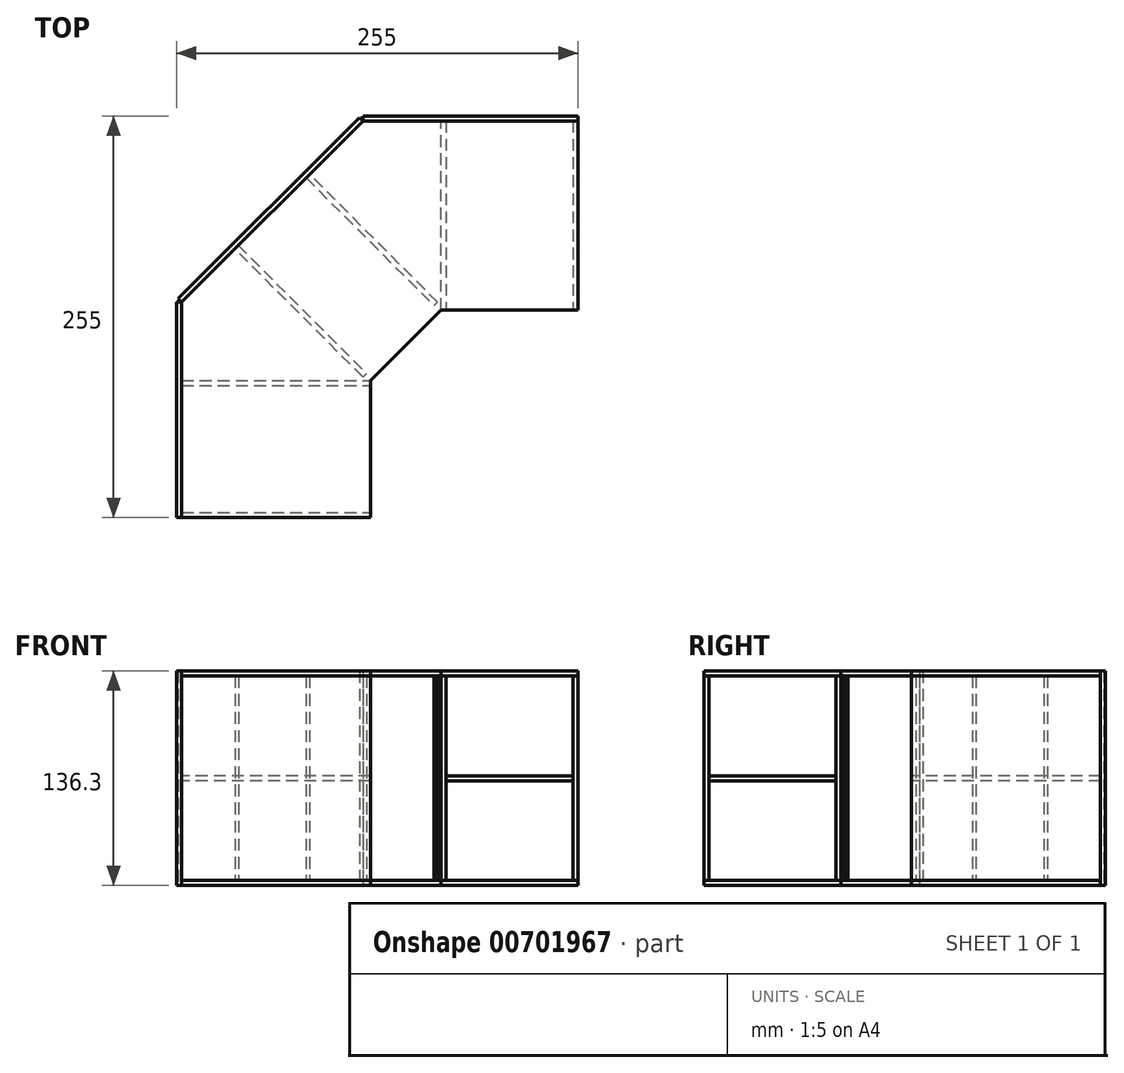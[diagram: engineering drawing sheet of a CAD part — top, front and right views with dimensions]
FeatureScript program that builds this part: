
annotation { "Feature Type Name" : "Feature", "Feature Type Description" : "" }
export const myFeature = defineFeature(function(context is Context, id is Id, definition is map)
    precondition{}
    {
        {
            assignVariable(context, id + "F0", {"name" : "x", "anyValue" : 3.15});
        }
        {
            var Q0;
            Q0=qCreatedBy(makeId("Top.planeOp"),FACE);
            var sketch = newSketch(context, id + "F1", { "sketchPlane" : qUnion([Q0])});
            skLineSegment(sketch, "E0", {"start": v(0, 0) * mm, "end": v(120, 0) * mm});
            skLineSegment(sketch, "E1", {"start": v(120, 0) * mm, "end": v(120, 87) * mm});
            skLineSegment(sketch, "E2", {"start": v(120, 87) * mm, "end": v(164.85, 131.85) * mm});
            skLineSegment(sketch, "E3", {"start": v(164.85, 131.85) * mm, "end": v(251.85, 131.85) * mm});
            skLineSegment(sketch, "E4", {"start": v(251.85, 131.85) * mm, "end": v(251.85, 251.85) * mm});
            skLineSegment(sketch, "E5", {"start": v(251.85, 251.85) * mm, "end": v(115.14, 251.85) * mm});
            skLineSegment(sketch, "E6", {"start": v(115.14, 251.85) * mm, "end": v(0, 136.7) * mm});
            skLineSegment(sketch, "E7", {"start": v(0, 136.7) * mm, "end": v(0, 0) * mm});
            skLineSegment(sketch, "E8", {"start": v(0, 136.7) * mm, "end": v(0, 251.85) * mm, "construction": true});
            skLineSegment(sketch, "E9", {"start": v(0, 251.85) * mm, "end": v(115.14, 251.85) * mm, "construction": true});
            skLineSegment(sketch, "E10", {"start": v(251.85, 131.85) * mm, "end": v(251.85, 0) * mm, "construction": true});
            skLineSegment(sketch, "E11", {"start": v(251.85, 0) * mm, "end": v(120, 0) * mm, "construction": true});
            skLineSegment(sketch, "E12", {"start": v(251.85, 0) * mm, "end": v(142.42, 109.42) * mm, "construction": true});
            skLineSegment(sketch, "E13", {"start": v(142.43, 109.42) * mm, "end": v(57.57, 194.28) * mm, "construction": true});
            skLineSegment(sketch, "E14", {"start": v(57.57, 194.28) * mm, "end": v(0, 251.85) * mm, "construction": true});
            skLineSegment(sketch, "E15.0", {"start": v(-3.15, 104.14) * mm, "end": v(-3.15, 0) * mm});
            skSolve(sketch);
        }
        {
            var Q0;
            Q0 = qSketchRegion(id + "F1", true);
            extrude(context, id + "F2", {"entities" : qUnion([Q0]), "depth" : (getVariable(context, 'x')) * mm, "offsetDistance" : 25 * mm});
        }
        {
            var Q0;
            Q0=makeQuery(id+"F2.opExtrude","SWEPT_FACE",FACE,{"disambiguationData":[OSD([sQuery(id+"F1.wireOp",EDGE,"E0")])]});
            var sketch = newSketch(context, id + "F3", { "sketchPlane" : qUnion([Q0])});
            skLineSegment(sketch, "E16.bottom", {"start": v(0, 0) * mm, "end": v(120, 0) * mm});
            skLineSegment(sketch, "E16.top", {"start": v(0, -130) * mm, "end": v(120, -130) * mm});
            skLineSegment(sketch, "E16.left", {"start": v(0, 0) * mm, "end": v(0, -130) * mm});
            skLineSegment(sketch, "E16.right", {"start": v(120, 0) * mm, "end": v(120, -130) * mm});
            skSolve(sketch);
        }
        {
            var Q0;
            Q0 = qSketchRegion(id + "F3", true);
            extrude(context, id + "F4", {"entities" : qUnion([Q0]), "oppositeDirection" : true, "depth" : (getVariable(context, 'x')) * mm, "offsetDistance" : 25 * mm});
        }
        {
            var Q0;
            Q0=makeQuery(id+"F4.opExtrude","SWEPT_BODY",BODY,{"disambiguationData":[OSD([sQuery(id+"F3.wireOp",EDGE,"E16.bottom"),sQuery(id+"F3.wireOp",EDGE,"E16.top"),sQuery(id+"F3.wireOp",EDGE,"E16.left"),sQuery(id+"F3.wireOp",EDGE,"E16.right")])]});
            transform(context, id + "F5", {"entities" : qUnion([Q0]), "transformType" : TransformType.TRANSLATION_3D, "dx" : 0 * mm, "dy" : 83.9 * mm, "dz" : 0 * mm, "makeCopy" : true});
        }
        {
            var Q0;
            Q0=makeQuery(id+"F2.opExtrude","SWEPT_FACE",FACE,{"disambiguationData":[OSD([sQuery(id+"F1.wireOp",EDGE,"E4")])]});
            var sketch = newSketch(context, id + "F6", { "sketchPlane" : qUnion([Q0])});
            skLineSegment(sketch, "E17.bottom", {"start": v(131.85, 0) * mm, "end": v(251.85, 0) * mm});
            skLineSegment(sketch, "E17.top", {"start": v(131.85, -130) * mm, "end": v(251.85, -130) * mm});
            skLineSegment(sketch, "E17.left", {"start": v(131.85, 0) * mm, "end": v(131.85, -130) * mm});
            skLineSegment(sketch, "E17.right", {"start": v(251.85, 0) * mm, "end": v(251.85, -130) * mm});
            skSolve(sketch);
        }
        {
            var Q0;
            Q0 = qSketchRegion(id + "F6", true);
            extrude(context, id + "F7", {"entities" : qUnion([Q0]), "oppositeDirection" : true, "depth" : (getVariable(context, 'x')) * mm, "offsetDistance" : 25 * mm});
        }
        {
            var Q0;
            Q0=makeQuery(id+"F7.opExtrude","SWEPT_BODY",BODY,{"disambiguationData":[OSD([sQuery(id+"F6.wireOp",EDGE,"E17.bottom"),sQuery(id+"F6.wireOp",EDGE,"E17.top"),sQuery(id+"F6.wireOp",EDGE,"E17.left"),sQuery(id+"F6.wireOp",EDGE,"E17.right")])]});
            transform(context, id + "F8", {"entities" : qUnion([Q0]), "transformType" : TransformType.TRANSLATION_3D, "dx" : -83.9 * mm, "dy" : 0 * mm, "dz" : 0 * mm, "makeCopy" : true});
        }
        {
            var Q0;
            Q0=makeQuery(id+"F2.opExtrude","SWEPT_BODY",BODY,{"disambiguationData":[OSD([sQuery(id+"F1.wireOp",EDGE,"E0"),sQuery(id+"F1.wireOp",EDGE,"E1"),sQuery(id+"F1.wireOp",EDGE,"E2"),sQuery(id+"F1.wireOp",EDGE,"E3"),sQuery(id+"F1.wireOp",EDGE,"E4"),sQuery(id+"F1.wireOp",EDGE,"E5"),sQuery(id+"F1.wireOp",EDGE,"E6"),sQuery(id+"F1.wireOp",EDGE,"E7")])]});
            transform(context, id + "F9", {"entities" : qUnion([Q0]), "transformType" : TransformType.TRANSLATION_3D, "dx" : 0 * mm, "dy" : 0 * mm, "dz" : (-130 - 3.15) * mm, "makeCopy" : true});
        }
        {
            var Q0;
            Q0=makeQuery(id+"F9.opPattern","COPY",FACE,{"derivedFrom":makeQuery(id+"F2.opExtrude","CAP_FACE",FACE,{"disambiguationData":[OSD([sQuery(id+"F1.wireOp",EDGE,"E0"),sQuery(id+"F1.wireOp",EDGE,"E1"),sQuery(id+"F1.wireOp",EDGE,"E2"),sQuery(id+"F1.wireOp",EDGE,"E3"),sQuery(id+"F1.wireOp",EDGE,"E4"),sQuery(id+"F1.wireOp",EDGE,"E5"),sQuery(id+"F1.wireOp",EDGE,"E6"),sQuery(id+"F1.wireOp",EDGE,"E7")])],"isStart":false}),"instanceName":"1"});
            cPlane(context, id + "F10", {"entities" : qUnion([Q0]), "cplaneType" : CPlaneType.OFFSET, "offset" : 63.42 * mm, "width" : 150 * mm, "height" : 150 * mm});
        }
        {
            var Q0;
            Q0=qCreatedBy(id+"F10.planeOp",FACE);
            var sketch = newSketch(context, id + "F11", { "sketchPlane" : qUnion([Q0])});
            skLineSegment(sketch, "E18.bottom", {"start": v(120, 3.15) * mm, "end": v(0, 3.15) * mm});
            skLineSegment(sketch, "E18.top", {"start": v(120, 83.9) * mm, "end": v(0, 83.9) * mm});
            skLineSegment(sketch, "E18.left", {"start": v(120, 3.15) * mm, "end": v(120, 83.9) * mm});
            skLineSegment(sketch, "E18.right", {"start": v(0, 3.15) * mm, "end": v(0, 83.9) * mm});
            skLineSegment(sketch, "E19.bottom", {"start": v(167.95, 251.85) * mm, "end": v(248.7, 251.85) * mm});
            skLineSegment(sketch, "E19.top", {"start": v(167.95, 131.85) * mm, "end": v(248.7, 131.85) * mm});
            skLineSegment(sketch, "E19.left", {"start": v(167.95, 251.85) * mm, "end": v(167.95, 131.85) * mm});
            skLineSegment(sketch, "E19.right", {"start": v(248.7, 251.85) * mm, "end": v(248.7, 131.85) * mm});
            skSolve(sketch);
        }
        {
            var Q0;
            Q0 = qSketchRegion(id + "F11", true);
            extrude(context, id + "F12", {"entities" : qUnion([Q0]), "depth" : (getVariable(context, 'x')) * mm, "offsetDistance" : 25 * mm});
        }
        {
            var Q0;
            Q0=makeQuery(id+"F9.opPattern","COPY",FACE,{"derivedFrom":makeQuery(id+"F2.opExtrude","CAP_FACE",FACE,{"disambiguationData":[OSD([sQuery(id+"F1.wireOp",EDGE,"E0"),sQuery(id+"F1.wireOp",EDGE,"E1"),sQuery(id+"F1.wireOp",EDGE,"E2"),sQuery(id+"F1.wireOp",EDGE,"E3"),sQuery(id+"F1.wireOp",EDGE,"E4"),sQuery(id+"F1.wireOp",EDGE,"E5"),sQuery(id+"F1.wireOp",EDGE,"E6"),sQuery(id+"F1.wireOp",EDGE,"E7")])],"isStart":false}),"instanceName":"1"});
            var sketch = newSketch(context, id + "F13", { "sketchPlane" : qUnion([Q0])});
            skLineSegment(sketch, "E20", {"start": v(117.4, 91.46) * mm, "end": v(36.08, 172.78) * mm});
            skLineSegment(sketch, "E21", {"start": v(36.08, 172.78) * mm, "end": v(33.85, 170.55) * mm});
            skLineSegment(sketch, "E22", {"start": v(33.85, 170.55) * mm, "end": v(115.17, 89.24) * mm});
            skLineSegment(sketch, "E23", {"start": v(115.17, 89.24) * mm, "end": v(117.4, 91.46) * mm});
            skLineSegment(sketch, "E24", {"start": v(117.4, 91.46) * mm, "end": v(120.93, 87.93) * mm, "construction": true});
            skLineSegment(sketch, "E25", {"start": v(142.42, 109.42) * mm, "end": v(57.57, 194.28) * mm, "construction": true});
            skLineSegment(sketch, "E26.MirrorCS", {"start": v(79.07, 215.77) * mm, "end": v(81.3, 218) * mm});
            skLineSegment(sketch, "E27.MirrorCS", {"start": v(162.61, 136.68) * mm, "end": v(160.39, 134.46) * mm});
            skLineSegment(sketch, "E28.MirrorCS", {"start": v(81.3, 218) * mm, "end": v(162.61, 136.68) * mm});
            skLineSegment(sketch, "E29.MirrorCS", {"start": v(160.39, 134.46) * mm, "end": v(79.07, 215.77) * mm});
            skSolve(sketch);
        }
        {
            var Q0;
            Q0 = qSketchRegion(id + "F13", true);
            var Q1;
            Q1=makeQuery(id+"F5.opPattern","COPY",FACE,{"derivedFrom":makeQuery(id+"F4.opExtrude","SWEPT_FACE",FACE,{"disambiguationData":[OSD([sQuery(id+"F3.wireOp",EDGE,"E16.bottom")])]}),"instanceName":"1"});
            extrude(context, id + "F14", {"entities" : qUnion([Q0]), "endBound" : BoundingType.UP_TO_SURFACE, "depth" : 25 * mm, "endBoundEntityFace" : qUnion([Q1]), "offsetDistance" : 25 * mm});
        }
        {
            var Q0;
            Q0=makeQuery(id+"F2.opExtrude","SWEPT_FACE",FACE,{"disambiguationData":[OSD([sQuery(id+"F1.wireOp",EDGE,"E7")])]});
            var sketch = newSketch(context, id + "F15", { "sketchPlane" : qUnion([Q0])});
            skLineSegment(sketch, "E30.bottom", {"start": v(0, 3.15) * mm, "end": v(-136.7, 3.15) * mm});
            skLineSegment(sketch, "E30.top", {"start": v(0, -133.15) * mm, "end": v(-136.7, -133.15) * mm});
            skLineSegment(sketch, "E30.left", {"start": v(0, 3.15) * mm, "end": v(0, -133.15) * mm});
            skLineSegment(sketch, "E30.right", {"start": v(-136.7, 3.15) * mm, "end": v(-136.7, -133.15) * mm});
            skSolve(sketch);
        }
        {
            var Q0;
            Q0 = qSketchRegion(id + "F15", true);
            extrude(context, id + "F16", {"entities" : qUnion([Q0]), "depth" : (getVariable(context, 'x')) * mm, "offsetDistance" : 25 * mm});
        }
        {
            var Q0;
            Q0=makeQuery(id+"F2.opExtrude","SWEPT_FACE",FACE,{"disambiguationData":[OSD([sQuery(id+"F1.wireOp",EDGE,"E5")])]});
            var sketch = newSketch(context, id + "F17", { "sketchPlane" : qUnion([Q0])});
            skLineSegment(sketch, "E31.bottom", {"start": v(-251.85, 3.15) * mm, "end": v(-115.14, 3.15) * mm});
            skLineSegment(sketch, "E31.top", {"start": v(-251.85, -133.15) * mm, "end": v(-115.14, -133.15) * mm});
            skLineSegment(sketch, "E31.left", {"start": v(-251.85, 3.15) * mm, "end": v(-251.85, -133.15) * mm});
            skLineSegment(sketch, "E31.right", {"start": v(-115.14, 3.15) * mm, "end": v(-115.14, -133.15) * mm});
            skSolve(sketch);
        }
        {
            var Q0;
            Q0 = qSketchRegion(id + "F17", true);
            extrude(context, id + "F18", {"entities" : qUnion([Q0]), "depth" : (getVariable(context, 'x')) * mm, "offsetDistance" : 25 * mm});
        }
        {
            var Q0;
            Q0=makeQuery(id+"F9.opPattern","COPY",FACE,{"derivedFrom":makeQuery(id+"F2.opExtrude","SWEPT_FACE",FACE,{"disambiguationData":[OSD([sQuery(id+"F1.wireOp",EDGE,"E6")])]}),"instanceName":"1"});
            var sketch = newSketch(context, id + "F19", { "sketchPlane" : qUnion([Q0])});
            skLineSegment(sketch, "E32.bottom", {"start": v(-259.5, 3.15) * mm, "end": v(-96.67, 3.15) * mm});
            skLineSegment(sketch, "E32.top", {"start": v(-259.5, -133.15) * mm, "end": v(-96.67, -133.15) * mm});
            skLineSegment(sketch, "E32.left", {"start": v(-259.5, 3.15) * mm, "end": v(-259.5, -133.15) * mm});
            skLineSegment(sketch, "E32.right", {"start": v(-96.67, 3.15) * mm, "end": v(-96.67, -133.15) * mm});
            skSolve(sketch);
        }
        {
            var Q0;
            Q0 = qSketchRegion(id + "F19", true);
            extrude(context, id + "F20", {"entities" : qUnion([Q0]), "depth" : (getVariable(context, 'x')) * mm, "offsetDistance" : 25 * mm});
        }
    });
